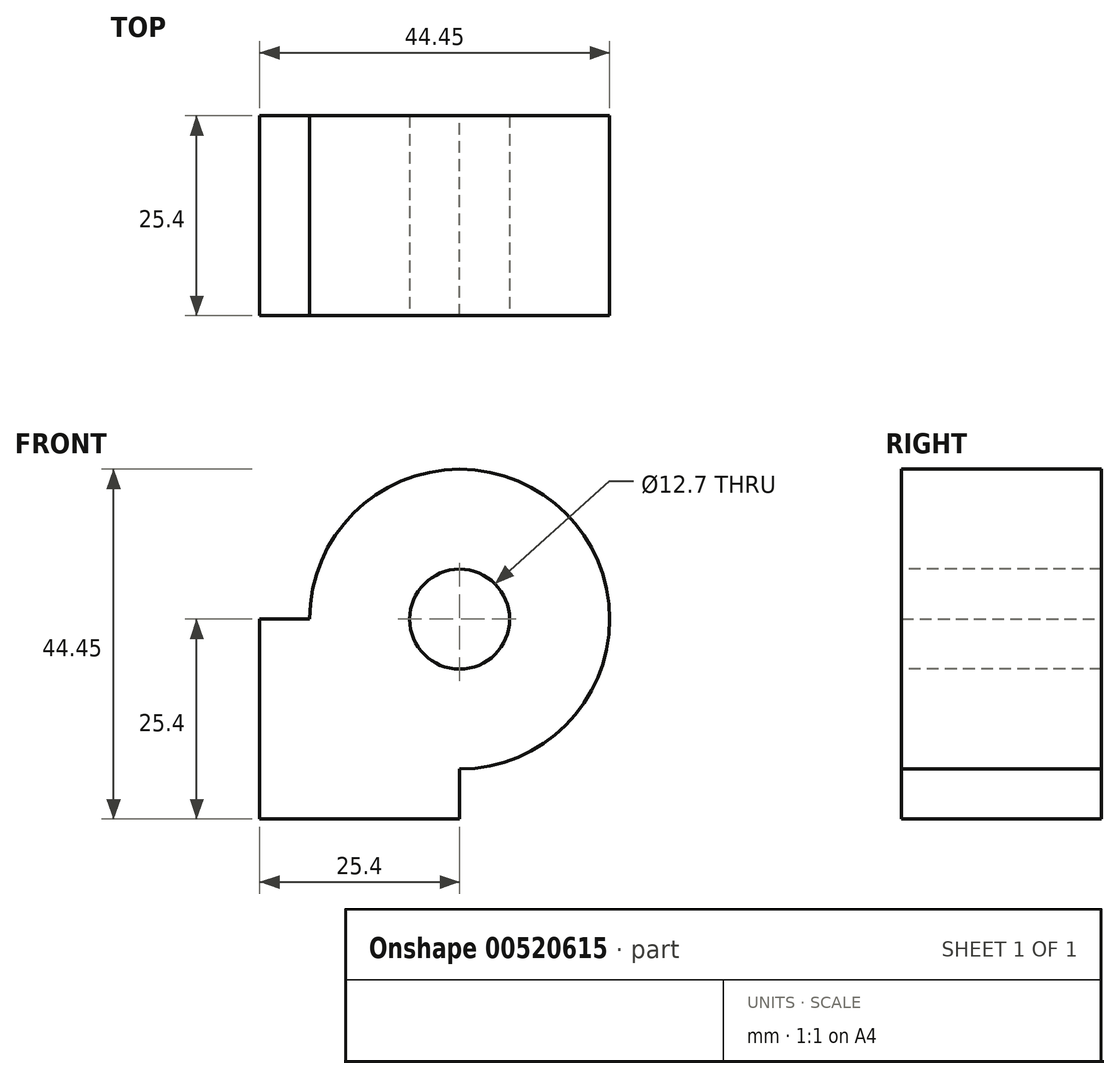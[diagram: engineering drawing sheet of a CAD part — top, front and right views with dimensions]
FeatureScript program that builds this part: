
annotation { "Feature Type Name" : "Feature", "Feature Type Description" : "" }
export const myFeature = defineFeature(function(context is Context, id is Id, definition is map)
    precondition{}
    {
        {
            var Q0;
            Q0=qCreatedBy(makeId("Front.planeOp"),FACE);
            var sketch = newSketch(context, id + "F0", { "sketchPlane" : qUnion([Q0])});
            skLineSegment(sketch, "E0", {"start": v(0, 0) * mm, "end": v(25.4, 0) * mm});
            skLineSegment(sketch, "E1", {"start": v(25.4, 0) * mm, "end": v(25.4, 6.35) * mm});
            skLineSegment(sketch, "E2", {"start": v(6.35, 25.4) * mm, "end": v(0, 25.4) * mm});
            skLineSegment(sketch, "E3", {"start": v(0, 25.4) * mm, "end": v(0, 0) * mm});
            skArc(sketch, "E4", {"start": v(25.4, 6.35) * mm, "mid": v(38.87, 38.87) * mm, "end": v(6.35, 25.4) * mm});
            skSolve(sketch);
        }
        {
            var Q0;
            Q0=makeQuery(id+"F0.imprint","IMPRINT",FACE,{"disambiguationData":[TD([[makeQuery(id+"F0.imprint","IMPRINT",EDGE,{"derivedFrom":sQuery(id+"F0.wireOp",EDGE,"E0")}),1.0]])]});
            extrude(context, id + "F1", {"entities" : qUnion([Q0]), "depth" : 25.4 * mm, "offsetDistance" : 25.4 * mm});
        }
        {
            var Q0;
            Q0=makeQuery(id+"F1.opExtrude","CAP_FACE",FACE,{"disambiguationData":[OSD([sQuery(id+"F0.wireOp",EDGE,"E0"),sQuery(id+"F0.wireOp",EDGE,"E1"),sQuery(id+"F0.wireOp",EDGE,"E2"),sQuery(id+"F0.wireOp",EDGE,"E3"),sQuery(id+"F0.wireOp",EDGE,"E4")])],"isStart":false});
            var sketch = newSketch(context, id + "F2", { "sketchPlane" : qUnion([Q0])});
            skCircle(sketch, "E5", {"center": v(25.4, 25.4) * mm, "radius": 6.35 * mm});
            skSolve(sketch);
        }
        {
            var Q0;
            Q0=makeQuery(id+"F2.imprint","IMPRINT",FACE,{"disambiguationData":[TD([[makeQuery(id+"F2.imprint","IMPRINT",EDGE,{"derivedFrom":sQuery(id+"F2.wireOp",EDGE,"E5")}),1.0]])]});
            extrude(context, id + "F3", {"entities" : qUnion([Q0]), "operationType" : NewBodyOperationType.REMOVE, "oppositeDirection" : true, "depth" : 25.4 * mm, "offsetDistance" : 25.4 * mm});
        }
    });
